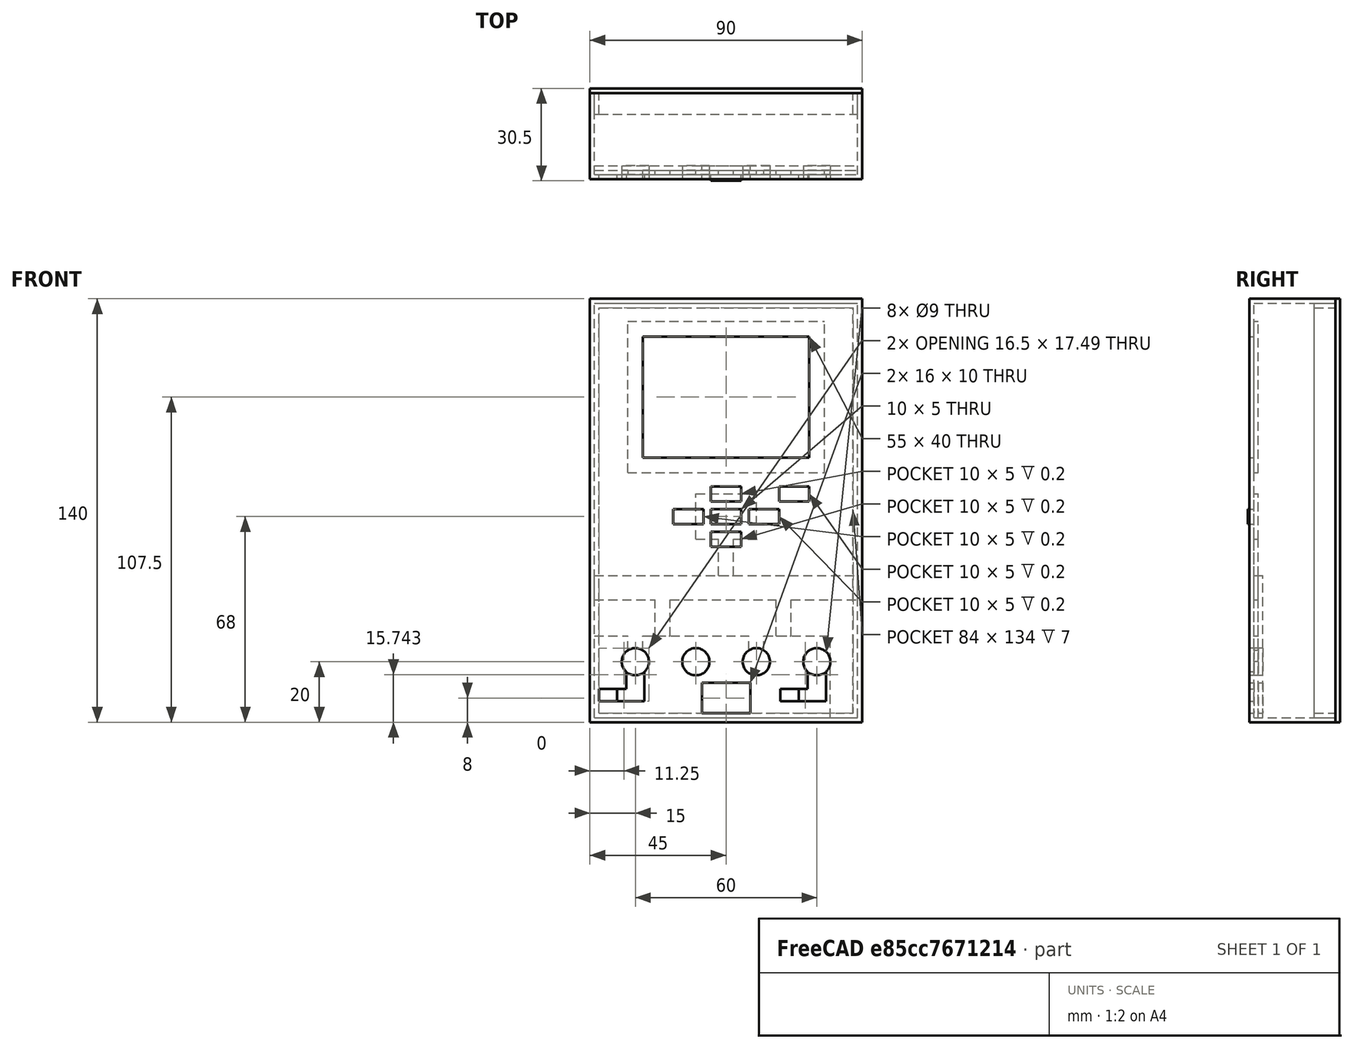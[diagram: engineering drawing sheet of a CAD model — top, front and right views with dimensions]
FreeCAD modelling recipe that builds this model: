
FCSTD DOCUMENT  (FreeCAD 0.17R7794 (Git) (Packman))
Label: External design
License: All rights reserved
LicenseURL: http://en.wikipedia.org/wiki/All_rights_reserved
objects: Part::Box×36, Part::Cylinder×12, Part::MultiFuse×12, Part::Cut×8
note: 68 computed .brp shape members not serialized (recipe doc carries the construction recipe); baked Part::Feature solids carry a one-line shape summary decoded from their .brp

FEATURE [Part::Box] Box  label="Cube"
  AttacherType = Attacher::AttachEngine3D
  Height = 140
  Length = 1.5
  Placement = pos=(0,1.5,0) rot=(0,0,1;0rad)
  Width = 27
FEATURE [Part::Box] Box001  label="Cube001"
  AttacherType = Attacher::AttachEngine3D
  Height = 140
  Length = 1.5
  Placement = pos=(88.5,1.5,0) rot=(0,0,1;0rad)
  Width = 27
FEATURE [Part::Box] Box002  label="Cube002"
  AttacherType = Attacher::AttachEngine3D
  Height = 1.5
  Length = 87
  Placement = pos=(1.5,1.5,0) rot=(0,0,1;0rad)
  Width = 27
FEATURE [Part::Box] Box004  label="Cube004"
  AttacherType = Attacher::AttachEngine3D
  Height = 1.5
  Length = 87
  Placement = pos=(1.5,1.5,138.5) rot=(0,0,1;0rad)
  Width = 27
FEATURE [Part::Box] Box005  label="Cube005"
  AttacherType = Attacher::AttachEngine3D
  Height = 1.5
  Length = 84
  Placement = pos=(3,21.5,137) rot=(0,0,1;0rad)
  Width = 7
FEATURE [Part::Box] Box006  label="Cube006"
  AttacherType = Attacher::AttachEngine3D
  Height = 137
  Length = 1.5
  Placement = pos=(1.5,21.5,1.5) rot=(0,0,1;0rad)
  Width = 7
FEATURE [Part::Box] Box007  label="Cube007"
  AttacherType = Attacher::AttachEngine3D
  Height = 140
  Length = 90
  Placement = pos=(0,28.5,0) rot=(0,0,1;0rad)
  Width = 1.5
FEATURE [Part::Box] Box008  label="Cube008"
  AttacherType = Attacher::AttachEngine3D
  Height = 137
  Length = 1.5
  Placement = pos=(87,21.5,1.5) rot=(0,0,1;0rad)
  Width = 7
FEATURE [Part::Box] Box009  label="Cube009"
  AttacherType = Attacher::AttachEngine3D
  Height = 1.5
  Length = 84
  Placement = pos=(3,21.5,1.5) rot=(0,0,1;0rad)
  Width = 7
FEATURE [Part::Box] Box011  label="Cube011"
  AttacherType = Attacher::AttachEngine3D
  Height = 50
  Length = 65
  Placement = pos=(12.5,1.5,82.5) rot=(0,0,1;0rad)
  Width = 1.5
FEATURE [Part::Cylinder] Cylinder
  Angle = 360
  AttacherType = Attacher::AttachEngine3D
  Height = 10
  Placement = pos=(15,5,20) rot=(1,0,0;1.5708rad)
  Radius = 4.5
FEATURE [Part::Cylinder] Cylinder001
  Angle = 360
  AttacherType = Attacher::AttachEngine3D
  Height = 10
  Placement = pos=(55,5,20) rot=(1,0,0;1.5708rad)
  Radius = 4.5
FEATURE [Part::Cylinder] Cylinder002
  Angle = 360
  AttacherType = Attacher::AttachEngine3D
  Height = 10
  Placement = pos=(35,5,20) rot=(1,0,0;1.5708rad)
  Radius = 4.5
FEATURE [Part::Cylinder] Cylinder003
  Angle = 360
  AttacherType = Attacher::AttachEngine3D
  Height = 10
  Placement = pos=(75,5,20) rot=(1,0,0;1.5708rad)
  Radius = 4.5
FEATURE [Part::Box] Box012  label="Cube012"
  AttacherType = Attacher::AttachEngine3D
  Height = 27
  Length = 78
  Placement = pos=(1.5,1.5,1.5) rot=(0,0,1;0rad)
  Width = 1.5
FEATURE [Part::MultiFuse] Fusion002
  Shapes = -> [Cylinder,Cylinder002,Cylinder001,Cylinder003]
FEATURE [Part::Cut] Cut002
  Base = -> Box012
  Tool = -> Fusion002
FEATURE [Part::Box] Box017  label="Cube017"
  AttacherType = Attacher::AttachEngine3D
  Height = 8
  Length = 87
  Placement = pos=(1.5,1.5,40.5) rot=(0,0,1;0rad)
  Width = 1.5
FEATURE [Part::Box] Box018  label="Cube018"
  AttacherType = Attacher::AttachEngine3D
  Height = 140
  Length = 90
  Width = 1.5
FEATURE [Part::Box] Box019  label="Cube019"
  AttacherType = Attacher::AttachEngine3D
  Height = 40
  Length = 55
  Placement = pos=(17.5,0,87.5) rot=(0,0,1;0rad)
  Width = 1.5
FEATURE [Part::Cut] Cut003
  Base = -> Box018
  Tool = -> Box019
FEATURE [Part::Cylinder] Cylinder004
  Angle = 360
  AttacherType = Attacher::AttachEngine3D
  Height = 10
  Placement = pos=(15,5,20) rot=(1,0,0;1.5708rad)
  Radius = 4.5
FEATURE [Part::Cylinder] Cylinder005
  Angle = 360
  AttacherType = Attacher::AttachEngine3D
  Height = 10
  Placement = pos=(55,5,20) rot=(1,0,0;1.5708rad)
  Radius = 4.5
FEATURE [Part::Cylinder] Cylinder006
  Angle = 360
  AttacherType = Attacher::AttachEngine3D
  Height = 10
  Placement = pos=(35,5,20) rot=(1,0,0;1.5708rad)
  Radius = 4.5
FEATURE [Part::Cylinder] Cylinder007
  Angle = 360
  AttacherType = Attacher::AttachEngine3D
  Height = 10
  Placement = pos=(75,5,20) rot=(1,0,0;1.5708rad)
  Radius = 4.5
FEATURE [Part::Box] Box020  label="Cube020"
  AttacherType = Attacher::AttachEngine3D
  Height = 10
  Length = 16
  Placement = pos=(37,-5,3) rot=(0,0,1;0rad)
  Width = 10
FEATURE [Part::MultiFuse] Fusion003
  Shapes = -> [Box020,Cylinder004,Cylinder006,Cylinder005,Cylinder007]
FEATURE [Part::Cut] Cut004
  Base = -> Cut003
  Tool = -> Fusion003
FEATURE [Part::MultiFuse] Fusion001
  Shapes = -> [Box005,Box008,Box007,Box009,Box006]
FEATURE [Part::MultiFuse] Fusion
  Shapes = -> [Box004,Box,Box002,Box001,Cut004]
FEATURE [Part::Box] Box021  label="Cube021"
  AttacherType = Attacher::AttachEngine3D
  Height = 47
  Length = 87
  Placement = pos=(1.5,3,1.5) rot=(0,0,1;0rad)
  Width = 1.5
FEATURE [Part::Cylinder] Cylinder008
  Angle = 360
  AttacherType = Attacher::AttachEngine3D
  Height = 10
  Placement = pos=(15,5,20) rot=(1,0,0;1.5708rad)
  Radius = 4.5
FEATURE [Part::Cylinder] Cylinder009
  Angle = 360
  AttacherType = Attacher::AttachEngine3D
  Height = 10
  Placement = pos=(55,5,20) rot=(1,0,0;1.5708rad)
  Radius = 4.5
FEATURE [Part::Cylinder] Cylinder010
  Angle = 360
  AttacherType = Attacher::AttachEngine3D
  Height = 10
  Placement = pos=(35,5,20) rot=(1,0,0;1.5708rad)
  Radius = 4.5
FEATURE [Part::Cylinder] Cylinder011
  Angle = 360
  AttacherType = Attacher::AttachEngine3D
  Height = 10
  Placement = pos=(75,5,20) rot=(1,0,0;1.5708rad)
  Radius = 4.5
FEATURE [Part::Box] Box023  label="Cube023"
  AttacherType = Attacher::AttachEngine3D
  Height = 10
  Length = 16
  Placement = pos=(37,-5,3) rot=(0,0,1;0rad)
  Width = 10
FEATURE [Part::MultiFuse] Fusion004
  Shapes = -> [Box023,Cylinder008,Cylinder010,Cylinder009,Cylinder011]
FEATURE [Part::Cut] Cut
  Base = -> Box021
  Tool = -> Fusion004
FEATURE [Part::Box] Box024  label="Cube024"
  AttacherType = Attacher::AttachEngine3D
  Height = 12
  Length = 5
  Placement = pos=(21.5,1.5,28.5) rot=(0,0,1;0rad)
  Width = 1.5
FEATURE [Part::Box] Box025  label="Cube025"
  AttacherType = Attacher::AttachEngine3D
  Height = 12
  Length = 5
  Placement = pos=(52.5,1.5,16.5) rot=(0,0,1;0rad)
  Width = 1.5
FEATURE [Part::Cut] Cut005
  Base = -> Cut002
  Tool = -> Box025
FEATURE [Part::Box] Box026  label="Cube026"
  AttacherType = Attacher::AttachEngine3D
  Height = 12
  Length = 5
  Placement = pos=(61.5,1.5,28.5) rot=(0,0,1;0rad)
  Width = 1.5
FEATURE [Part::Box] Box027  label="Cube027"
  AttacherType = Attacher::AttachEngine3D
  Height = 12
  Length = 5
  Placement = pos=(12.5,1.5,16.5) rot=(0,0,1;0rad)
  Width = 1.5
FEATURE [Part::Cut] Cut006
  Base = -> Cut005
  Tool = -> Box027
FEATURE [Part::Box] Box028  label="Cube028"
  AttacherType = Attacher::AttachEngine3D
  Height = 4
  Length = 6
  Placement = pos=(3,0,7) rot=(0,0,1;0rad)
  Width = 1.5
FEATURE [Part::Box] Box029  label="Cube029"
  AttacherType = Attacher::AttachEngine3D
  Height = 4
  Length = 15
  Placement = pos=(3,0,7) rot=(0,0,1;0rad)
  Width = 1.5
FEATURE [Part::Box] Box030  label="Cube030"
  AttacherType = Attacher::AttachEngine3D
  Height = 12
  Length = 6
  Placement = pos=(12,0,11) rot=(0,0,1;0rad)
  Width = 1.5
FEATURE [Part::MultiFuse] Fusion005
  Shapes = -> [Box029,Box030]
FEATURE [Part::Box] Box031  label="Cube031"
  AttacherType = Attacher::AttachEngine3D
  Height = 4
  Length = 6
  Placement = pos=(63,0,7) rot=(0,0,1;0rad)
  Width = 1.5
FEATURE [Part::Box] Box032  label="Cube032"
  AttacherType = Attacher::AttachEngine3D
  Height = 4
  Length = 15
  Placement = pos=(63,0,7) rot=(0,0,1;0rad)
  Width = 1.5
FEATURE [Part::Box] Box033  label="Cube033"
  AttacherType = Attacher::AttachEngine3D
  Height = 12
  Length = 6
  Placement = pos=(72,0,11) rot=(0,0,1;0rad)
  Width = 1.5
FEATURE [Part::MultiFuse] Fusion006
  Shapes = -> [Box032,Box033]
FEATURE [Part::MultiFuse] Fusion007
  Shapes = -> [Fusion005,Fusion006]
FEATURE [Part::Cut] Cut007
  Base = -> Fusion
  Tool = -> Fusion007
FEATURE [Part::MultiFuse] Fusion008
  Shapes = -> [Cut006,Box028,Box031]
FEATURE [Part::Box] Box034  label="Cube034"
  AttacherType = Attacher::AttachEngine3D
  Height = 5
  Length = 10
  Placement = pos=(40,0,58) rot=(0,0,1;0rad)
  Width = 0.2
FEATURE [Part::Box] Box035  label="Cube035"
  AttacherType = Attacher::AttachEngine3D
  Height = 5
  Length = 10
  Placement = pos=(40,0,73) rot=(0,0,1;0rad)
  Width = 0.2
FEATURE [Part::Box] Box036  label="Cube036"
  AttacherType = Attacher::AttachEngine3D
  Height = 5
  Length = 10
  Placement = pos=(27.5,0,65.5) rot=(0,0,1;0rad)
  Width = 0.2
FEATURE [Part::Box] Box037  label="Cube037"
  AttacherType = Attacher::AttachEngine3D
  Height = 5
  Length = 10
  Placement = pos=(52.5,0,65.5) rot=(0,0,1;0rad)
  Width = 0.2
FEATURE [Part::Box] Box038  label="Cube038"
  AttacherType = Attacher::AttachEngine3D
  Height = 5
  Length = 10
  Placement = pos=(40,0,65.5) rot=(0,0,1;0rad)
  Width = 1.5
FEATURE [Part::Box] Box039  label="Cube039"
  AttacherType = Attacher::AttachEngine3D
  Height = 5
  Length = 10
  Placement = pos=(40,-0.5,65.5) rot=(0,0,1;0rad)
  Width = 2
FEATURE [Part::Box] Box040  label="Cube040"
  AttacherType = Attacher::AttachEngine3D
  Height = 15
  Length = 20
  Placement = pos=(35,1.5,60.5) rot=(0,0,1;0rad)
  Width = 1.5
FEATURE [Part::Box] Box041  label="Cube041"
  AttacherType = Attacher::AttachEngine3D
  Height = 12
  Length = 5
  Placement = pos=(42.5,1.5,48.5) rot=(0,0,1;0rad)
  Width = 1.5
FEATURE [Part::MultiFuse] Fusion010
  Shapes = -> [Box039,Box041,Box040]
FEATURE [Part::MultiFuse] Fusion011
  Shapes = -> [Box017,Box026,Box024]
FEATURE [Part::Box] Box042  label="Cube042"
  AttacherType = Attacher::AttachEngine3D
  Height = 5
  Length = 10
  Placement = pos=(62.5,0,73) rot=(0,0,1;0rad)
  Width = 0.2
FEATURE [Part::MultiFuse] Fusion012
  Shapes = -> [Box042,Box034,Box035,Box036,Box037,Box038]
FEATURE [Part::Cut] Cut008
  Base = -> Cut007
  Tool = -> Fusion012
